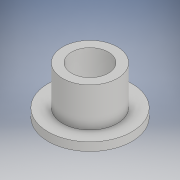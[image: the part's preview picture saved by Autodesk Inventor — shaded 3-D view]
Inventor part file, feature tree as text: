
AUTODESK INVENTOR PART (.ipt)
format: ipt  version: 2017 (Build 210142000, 142)  size: 112,128 bytes
history: native  units: mm
features: extrude x3, sketch x3, other x1
ambient origin geometry x8: Origin, YZ Plane, XZ Plane, XY Plane, X Axis, Y Axis, Z Axis, Center Point
bodies: Body1 (feature_tree)
feature tree (7):
  other  "Твердое тело1"
  extrude  "Выдавливание1"  Depth=15.0mm
  extrude  "Выдавливание2"  Depth=1.5mm TaperAngle=0.0deg
  extrude  "Выдавливание4"  Depth=9.8mm
  sketch  "Эскиз1"
  sketch  "Эскиз2"
  sketch  "Эскиз4"
